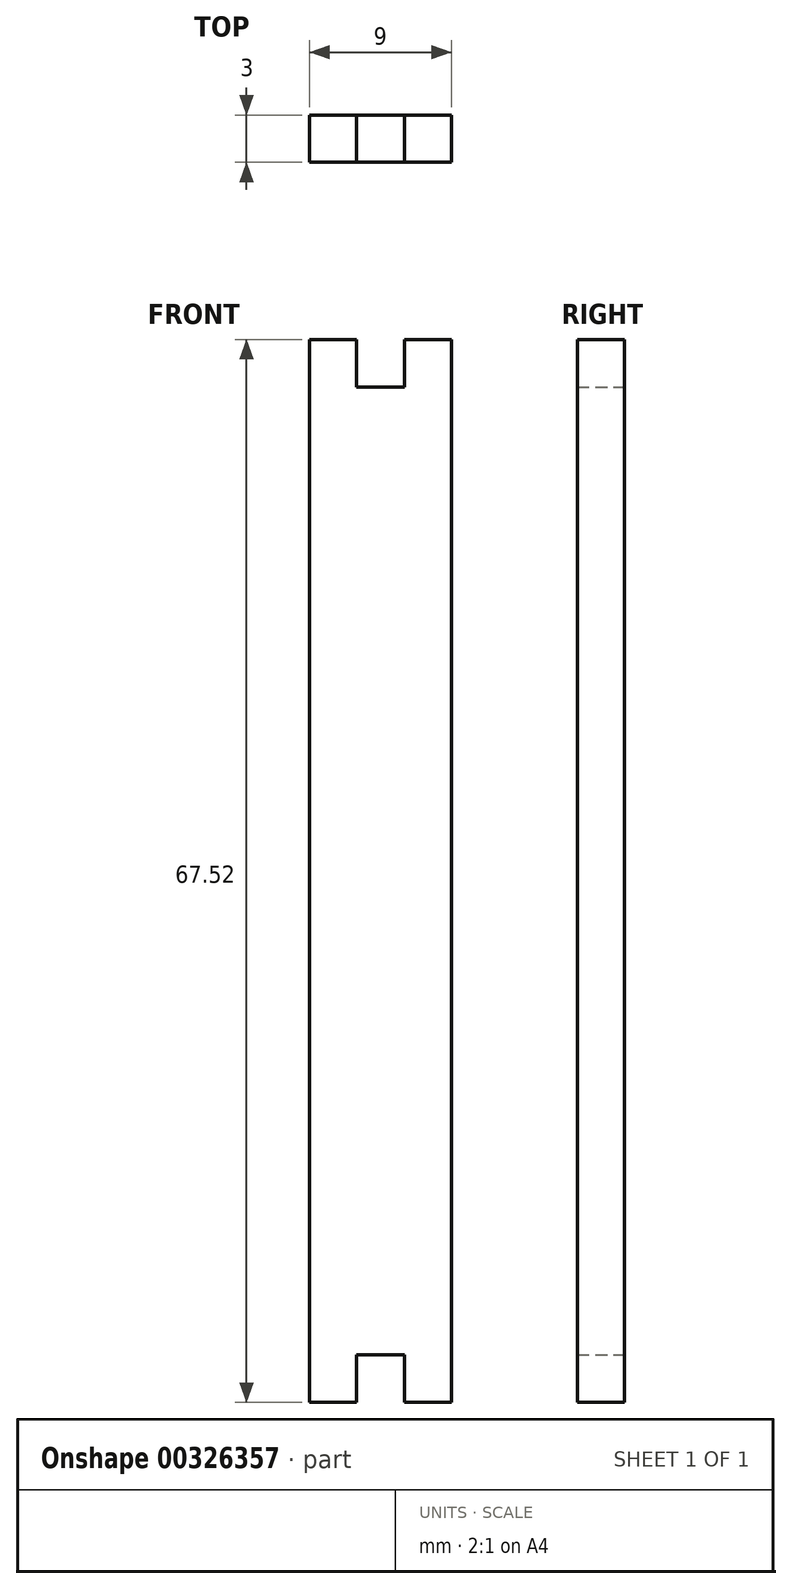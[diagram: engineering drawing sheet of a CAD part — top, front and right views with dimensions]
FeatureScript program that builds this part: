
annotation { "Feature Type Name" : "Feature", "Feature Type Description" : "" }
export const myFeature = defineFeature(function(context is Context, id is Id, definition is map)
    precondition{}
    {
        {
            var Q0;
            Q0=qCreatedBy(makeId("Front.planeOp"),FACE);
            var sketch = newSketch(context, id + "F0", { "sketchPlane" : qUnion([Q0])});
            skLineSegment(sketch, "E0", {"start": v(16.2, 33.76) * mm, "end": v(16.2, -33.76) * mm});
            skLineSegment(sketch, "E1", {"start": v(16.2, -33.76) * mm, "end": v(13.22, -33.76) * mm});
            skLineSegment(sketch, "E2", {"start": v(13.22, -33.76) * mm, "end": v(13.22, -30.74) * mm});
            skLineSegment(sketch, "E3", {"start": v(13.22, -30.74) * mm, "end": v(10.18, -30.74) * mm});
            skLineSegment(sketch, "E4", {"start": v(10.18, -30.74) * mm, "end": v(10.18, -33.76) * mm});
            skLineSegment(sketch, "E5", {"start": v(10.18, -33.76) * mm, "end": v(7.2, -33.76) * mm});
            skLineSegment(sketch, "E6", {"start": v(7.2, -33.76) * mm, "end": v(7.2, 33.76) * mm});
            skLineSegment(sketch, "E7", {"start": v(7.2, 33.76) * mm, "end": v(10.18, 33.76) * mm});
            skLineSegment(sketch, "E8", {"start": v(10.18, 33.76) * mm, "end": v(10.18, 30.74) * mm});
            skLineSegment(sketch, "E9", {"start": v(10.18, 30.74) * mm, "end": v(13.22, 30.74) * mm});
            skLineSegment(sketch, "E10", {"start": v(13.22, 30.74) * mm, "end": v(13.22, 33.76) * mm});
            skLineSegment(sketch, "E11", {"start": v(13.22, 33.76) * mm, "end": v(16.2, 33.76) * mm});
            skSolve(sketch);
        }
        {
            var Q0;
            Q0=makeQuery(id+"F0.imprint","IMPRINT",FACE,{"disambiguationData":[TD([[makeQuery(id+"F0.imprint","IMPRINT",EDGE,{"derivedFrom":sQuery(id+"F0.wireOp",EDGE,"E0")}),-1.0]])]});
            extrude(context, id + "F1", {"entities" : qUnion([Q0]), "depth" : 3 * mm});
        }
    });
